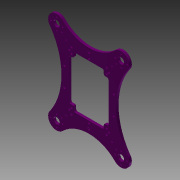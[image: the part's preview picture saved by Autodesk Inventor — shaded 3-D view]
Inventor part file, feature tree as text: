
AUTODESK INVENTOR PART (.ipt)
format: ipt  version: 2015 (Build 190159000, 159)  size: 403,456 bytes
history: native  units: mm
features: sketch x4, extrude x3
ambient origin geometry x8: Origin, YZ Plane, XZ Plane, XY Plane, X Axis, Y Axis, Z Axis, Center Point
bodies: Solid1 (feature_tree)
feature tree (7):
  extrude  "Extrusion1"  Depth=2.5mm
  extrude  "Extrusion2"  Depth=2.5mm
  extrude  "Extrusion3"  Depth=10.0mm
  sketch  "Sketch4"  dims[d21=2.5mm d22=2.5mm d23=9.0mm d26=29.0mm d30=2.0mm d31=2.0mm d34=3.5mm d35=0.0mm d40=2.5mm d41=0.0mm d42=9.0mm d43=9.0mm d44=9.0mm d45=9.0mm d46=2.5mm d50=10.0mm d51=0.0mm d52=68.48mm d53=51.000004mm]
  sketch  "Sketch1"  dims[d2=4.625mm d3=3.5mm d4=3.5mm d10=3.5mm d15=2.5mm]
  sketch  "Sketch2"  dims[d16=2.5mm d17=2.5mm]
  sketch  "Sketch3"  dims[d18=2.5mm d20=10.0mm]
